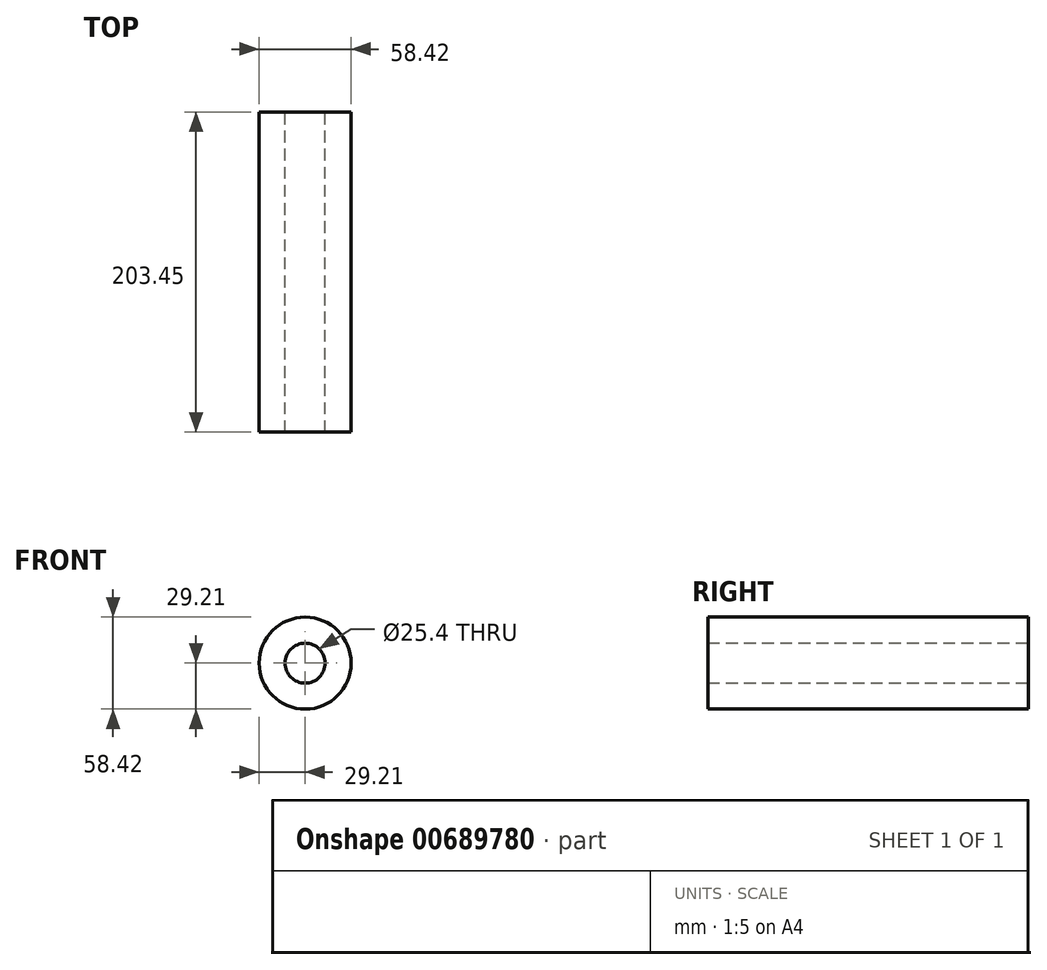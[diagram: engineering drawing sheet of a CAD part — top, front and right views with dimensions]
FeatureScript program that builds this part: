
annotation { "Feature Type Name" : "Feature", "Feature Type Description" : "" }
export const myFeature = defineFeature(function(context is Context, id is Id, definition is map)
    precondition{}
    {
        {
            var Q0;
            Q0=qCreatedBy(makeId("Front.planeOp"),FACE);
            var sketch = newSketch(context, id + "F0", { "sketchPlane" : qUnion([Q0])});
            skCircle(sketch, "E0", {"center": v(0, 0) * mm, "radius": 29.21 * mm});
            skSolve(sketch);
        }
        {
            var Q0;
            Q0=makeQuery(id+"F0.imprint","IMPRINT",FACE,{"disambiguationData":[TD([[makeQuery(id+"F0.imprint","IMPRINT",EDGE,{"derivedFrom":sQuery(id+"F0.wireOp",EDGE,"E0")}),1.0]])]});
            extrude(context, id + "F1", {"entities" : qUnion([Q0]), "oppositeDirection" : true, "depth" : 203.45 * mm, "offsetDistance" : 25.4 * mm});
        }
        {
            var Q0;
            Q0=makeQuery(id+"F1.opExtrude","CAP_FACE",FACE,{"disambiguationData":[OSD([sQuery(id+"F0.wireOp",EDGE,"E0")])],"isStart":true});
            var sketch = newSketch(context, id + "F2", { "sketchPlane" : qUnion([Q0])});
            skCircle(sketch, "E1", {"center": v(0, 0) * mm, "radius": 12.7 * mm});
            skSolve(sketch);
        }
        {
            var Q0;
            Q0=sQuery(id+"F2.wireOp",VERTEX,"E1.center");
            var Q1;
            Q1=makeQuery(id+"F1.opExtrude","SWEPT_BODY",BODY,{"disambiguationData":[OSD([sQuery(id+"F0.wireOp",EDGE,"E0")])]});
            hole(context, id + "F3", {"style" : HoleStyle.SIMPLE, "endStyle" : HoleEndStyle.THROUGH, "holeDiameter" : 25.4 * mm, "majorDiameter" : 6.35 * mm, "isTappedThrough" : true, "tappedDepth" : 12.7 * mm, "tapClearance" : 3, "locations" : qUnion([Q0]), "scope" : qUnion([Q1]), "startStyle" : HoleStartStyle.PART});
        }
    });
